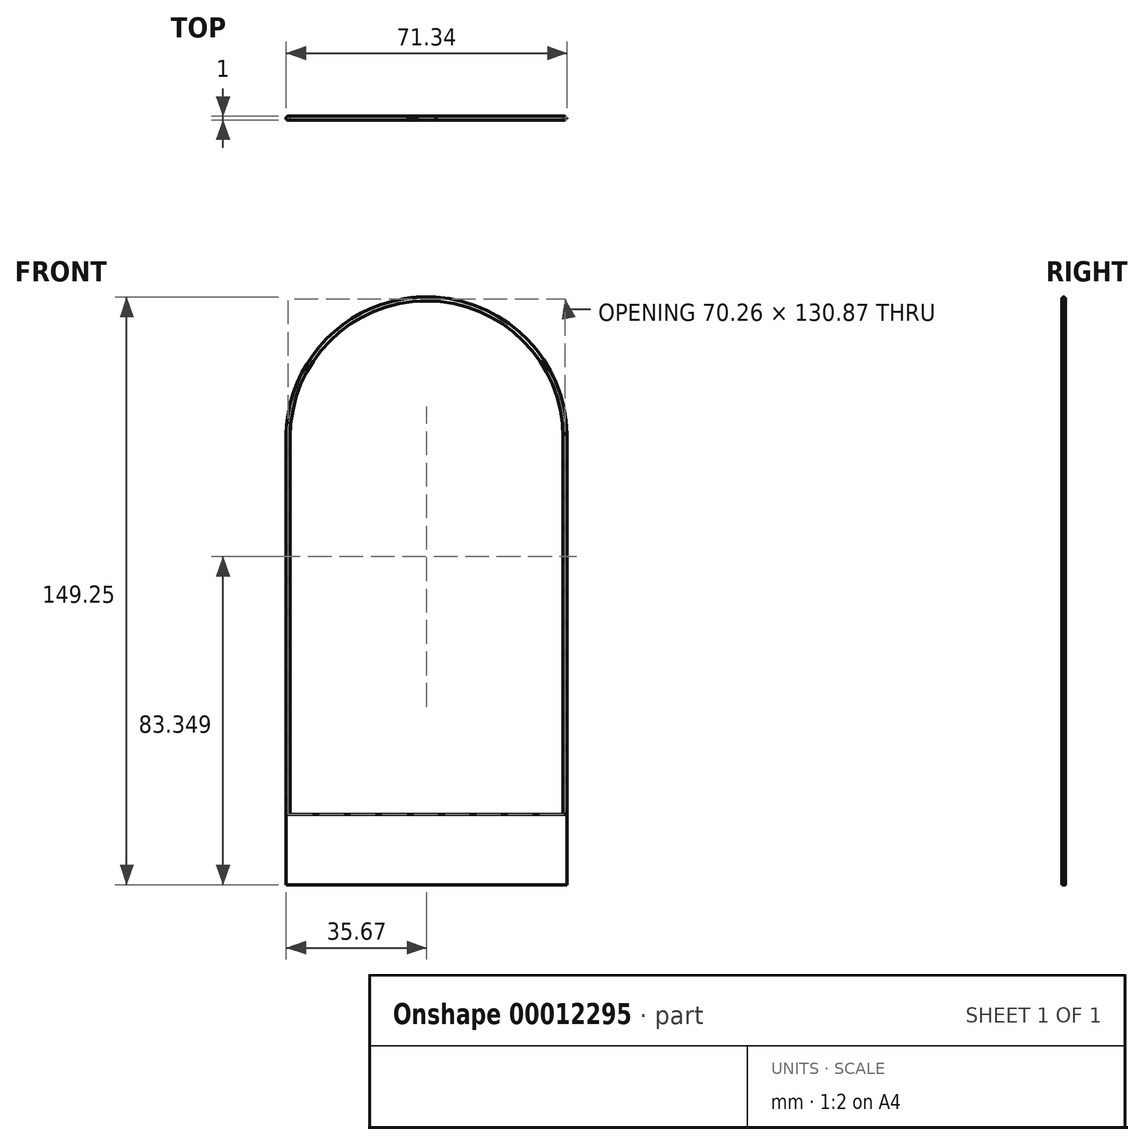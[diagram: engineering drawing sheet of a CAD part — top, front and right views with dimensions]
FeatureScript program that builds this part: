
annotation { "Feature Type Name" : "Feature", "Feature Type Description" : "" }
export const myFeature = defineFeature(function(context is Context, id is Id, definition is map)
    precondition{}
    {
        {
            var Q0;
            Q0=qCreatedBy(makeId("Front.planeOp"),FACE);
            var sketch = newSketch(context, id + "F0", { "sketchPlane" : qUnion([Q0])});
            skArc(sketch, "E0", {"start": v(35.67, 28.1) * mm, "mid": v(0, 64.7) * mm, "end": v(-35.67, 28.1) * mm});
            skLineSegment(sketch, "E1.rect.top", {"start": v(35.67, 64.61) * mm, "end": v(-35.67, 64.61) * mm});
            skLineSegment(sketch, "E1.rect.left", {"start": v(35.67, -6.58) * mm, "end": v(35.67, 28.1) * mm});
            skLineSegment(sketch, "E1.rect.right", {"start": v(-35.67, -6.58) * mm, "end": v(-35.67, 64.61) * mm});
            skLineSegment(sketch, "E2", {"start": v(-35.67, -6.58) * mm, "end": v(-35.67, -84.64) * mm});
            skLineSegment(sketch, "E3", {"start": v(-35.67, -84.64) * mm, "end": v(35.67, -84.64) * mm});
            skLineSegment(sketch, "E4", {"start": v(35.67, -84.64) * mm, "end": v(35.67, -6.58) * mm});
            skLineSegment(sketch, "E5", {"start": v(-35.67, -66.73) * mm, "end": v(35.67, -66.73) * mm});
            skLineSegment(sketch, "E6", {"start": v(-35.67, -6.58) * mm, "end": v(-35.67, 29.02) * mm});
            skLineSegment(sketch, "E7", {"start": v(35.67, -6.58) * mm, "end": v(35.67, 29.02) * mm});
            skArc(sketch, "E8.0", {"start": v(34.68, 29.02) * mm, "mid": v(0, 63.7) * mm, "end": v(-34.68, 29.02) * mm});
            skLineSegment(sketch, "E9", {"start": v(-34.68, 29.02) * mm, "end": v(-34.68, -66.73) * mm});
            skLineSegment(sketch, "E10", {"start": v(-35.67, 29.02) * mm, "end": v(35.67, 29.02) * mm});
            skLineSegment(sketch, "E11", {"start": v(34.68, 29.02) * mm, "end": v(34.68, -66.73) * mm});
            skLineSegment(sketch, "E12.trimOffspring", {"start": v(35.67, 29.02) * mm, "end": v(35.67, 64.61) * mm});
            skSolve(sketch);
        }
        {
            var Q0;
            {var subQ0=sQuery(id+"F0.wireOp",EDGE,"E11");Q0=makeQuery(id+"F0.imprint","IMPRINT",FACE,{"disambiguationData":[TD([[makeQuery(id+"F0.imprint","IMPRINT",EDGE,{"derivedFrom":subQ0}),1.0]])]});}
            var Q1;
            {var subQ5=sQuery(id+"F0.wireOp",EDGE,"E8.0");Q1=makeQuery(id+"F0.imprint","IMPRINT",FACE,{"disambiguationData":[TD([[makeQuery(id+"F0.imprint","IMPRINT",EDGE,{"derivedFrom":subQ5}),-1.0]])]});}
            var Q2;
            {var subQ1=sQuery(id+"F0.wireOp",EDGE,"E9");Q2=makeQuery(id+"F0.imprint","IMPRINT",FACE,{"disambiguationData":[TD([[makeQuery(id+"F0.imprint","IMPRINT",EDGE,{"derivedFrom":subQ1}),-1.0]])]});}
            var Q3;
            {var subQ7=sQuery(id+"F0.wireOp",EDGE,"E3");Q3=makeQuery(id+"F0.imprint","IMPRINT",FACE,{"disambiguationData":[TD([[makeQuery(id+"F0.imprint","IMPRINT",EDGE,{"derivedFrom":subQ7}),1.0]])]});}
            extrude(context, id + "F1", {"entities" : qUnion([Q0, Q1, Q2, Q3]), "depth" : 1 * mm});
        }
        {
            var Q0;
            {var subQ7=sQuery(id+"F0.wireOp",EDGE,"E3");Q0=makeQuery(id+"F0.imprint","IMPRINT",FACE,{"disambiguationData":[TD([[makeQuery(id+"F0.imprint","IMPRINT",EDGE,{"derivedFrom":subQ7}),1.0]])]});}
            extrude(context, id + "F2", {"entities" : qUnion([Q0]), "operationType" : NewBodyOperationType.ADD, "depth" : 1 * mm});
        }
        {
            var Q0;
            Q0=makeQuery(id+"F1.opExtrude","CAP_EDGE",EDGE,{"disambiguationData":[OSD([sQuery(id+"F0.wireOp",EDGE,"E11")])],"isStart":false});
            var Q1;
            Q1=makeQuery(id+"F1.opExtrude","CAP_EDGE",EDGE,{"disambiguationData":[OSD([sQuery(id+"F0.wireOp",EDGE,"E4"),sQuery(id+"F0.wireOp",EDGE,"E7"),sQuery(id+"F0.wireOp",EDGE,"E12.trimOffspring")])],"isStart":false});
            var Q2;
            Q2=makeQuery(id+"F1.opExtrude","CAP_EDGE",EDGE,{"disambiguationData":[OSD([sQuery(id+"F0.wireOp",EDGE,"E4"),sQuery(id+"F0.wireOp",EDGE,"E7"),sQuery(id+"F0.wireOp",EDGE,"E12.trimOffspring")])],"isStart":true});
            var Q3;
            Q3=makeQuery(id+"F1.opExtrude","CAP_EDGE",EDGE,{"disambiguationData":[OSD([sQuery(id+"F0.wireOp",EDGE,"E11")])],"isStart":true});
            var Q4;
            {var subQ0=sQuery(id+"F0.wireOp",EDGE,"E0");Q4=makeQuery(id+"F1.opExtrude","CAP_EDGE",EDGE,{"disambiguationData":[OSD([subQ0]),TDD([makeQuery(id+"F0.imprint","IMPRINT",EDGE,{"disambiguationData":[TD([[makeQuery(id+"F0.imprint","INTERSECT",VERTEX,{"derivedFrom":[subQ0,sQuery(id+"F0.wireOp",EDGE,"E12.trimOffspring")]}),-1.0]])],"derivedFrom":subQ0})])],"isStart":false});}
            var Q5;
            Q5=makeQuery(id+"F1.opExtrude","CAP_EDGE",EDGE,{"disambiguationData":[OSD([sQuery(id+"F0.wireOp",EDGE,"E8.0")])],"isStart":false});
            var Q6;
            Q6=makeQuery(id+"F1.opExtrude","CAP_EDGE",EDGE,{"disambiguationData":[OSD([sQuery(id+"F0.wireOp",EDGE,"E1.rect.top")])],"isStart":false});
            var Q7;
            {var subQ0=sQuery(id+"F0.wireOp",EDGE,"E0");Q7=makeQuery(id+"F1.opExtrude","CAP_EDGE",EDGE,{"disambiguationData":[OSD([subQ0]),TDD([makeQuery(id+"F0.imprint","IMPRINT",EDGE,{"disambiguationData":[TD([[makeQuery(id+"F0.imprint","INTERSECT",VERTEX,{"derivedFrom":[subQ0,sQuery(id+"F0.wireOp",EDGE,"E12.trimOffspring")]}),-1.0]])],"derivedFrom":subQ0})])],"isStart":true});}
            var Q8;
            Q8=makeQuery(id+"F1.opExtrude","CAP_EDGE",EDGE,{"disambiguationData":[OSD([sQuery(id+"F0.wireOp",EDGE,"E1.rect.top")])],"isStart":true});
            var Q9;
            {var subQ0=sQuery(id+"F0.wireOp",EDGE,"E0");Q9=makeQuery(id+"F1.opExtrude","CAP_EDGE",EDGE,{"disambiguationData":[OSD([subQ0]),TDD([makeQuery(id+"F0.imprint","IMPRINT",EDGE,{"disambiguationData":[TD([[makeQuery(id+"F0.imprint","INTERSECT",VERTEX,{"disambiguationData":[OD(1.0)],"derivedFrom":[subQ0,sQuery(id+"F0.wireOp",EDGE,"E1.rect.top")]}),-1.0]])],"derivedFrom":subQ0})])],"isStart":true});}
            var Q10;
            {var subQ0=sQuery(id+"F0.wireOp",EDGE,"E0");Q10=makeQuery(id+"F1.opExtrude","CAP_EDGE",EDGE,{"disambiguationData":[OSD([subQ0]),TDD([makeQuery(id+"F0.imprint","IMPRINT",EDGE,{"disambiguationData":[TD([[makeQuery(id+"F0.imprint","INTERSECT",VERTEX,{"disambiguationData":[OD(1.0)],"derivedFrom":[subQ0,sQuery(id+"F0.wireOp",EDGE,"E1.rect.top")]}),-1.0]])],"derivedFrom":subQ0})])],"isStart":false});}
            var Q11;
            Q11=makeQuery(id+"F1.opExtrude","CAP_EDGE",EDGE,{"disambiguationData":[OSD([sQuery(id+"F0.wireOp",EDGE,"E1.rect.right"),sQuery(id+"F0.wireOp",EDGE,"E2"),sQuery(id+"F0.wireOp",EDGE,"E6")])],"isStart":false});
            var Q12;
            Q12=makeQuery(id+"F1.opExtrude","CAP_EDGE",EDGE,{"disambiguationData":[OSD([sQuery(id+"F0.wireOp",EDGE,"E9")])],"isStart":false});
            var Q13;
            Q13=makeQuery(id+"F1.opExtrude","CAP_EDGE",EDGE,{"disambiguationData":[OSD([sQuery(id+"F0.wireOp",EDGE,"E1.rect.right"),sQuery(id+"F0.wireOp",EDGE,"E2"),sQuery(id+"F0.wireOp",EDGE,"E6")])],"isStart":true});
            var Q14;
            Q14=makeQuery(id+"F1.opExtrude","CAP_EDGE",EDGE,{"disambiguationData":[OSD([sQuery(id+"F0.wireOp",EDGE,"E9")])],"isStart":true});
            var Q15;
            Q15=makeQuery(id+"F1.opExtrude","CAP_EDGE",EDGE,{"disambiguationData":[OSD([sQuery(id+"F0.wireOp",EDGE,"E8.0")])],"isStart":true});
            fillet(context, id + "F3", {"entities" : qUnion([Q0, Q1, Q2, Q3, Q4, Q5, Q6, Q7, Q8, Q9, Q10, Q11, Q12, Q13, Q14, Q15]), "radius" : .45 * mm, "tangentPropagation" : true, "allowEdgeOverflow" : false});
        }
    });
